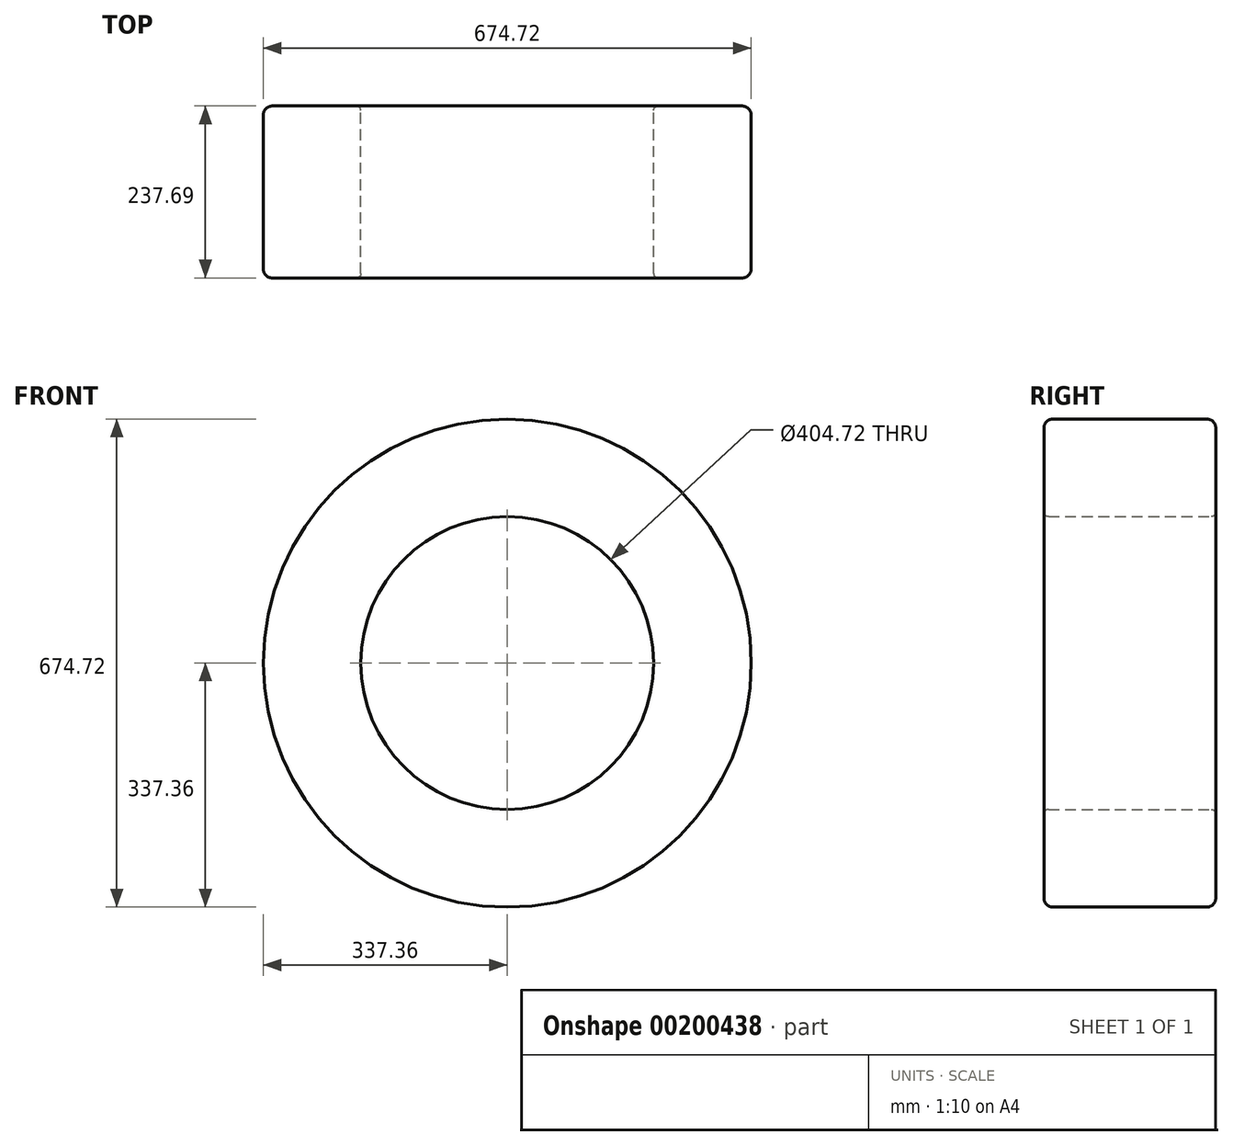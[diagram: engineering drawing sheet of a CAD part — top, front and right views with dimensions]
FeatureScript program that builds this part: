
annotation { "Feature Type Name" : "Feature", "Feature Type Description" : "" }
export const myFeature = defineFeature(function(context is Context, id is Id, definition is map)
    precondition{}
    {
        {
            var Q0;
            Q0=qCreatedBy(makeId("Front.planeOp"),FACE);
            var sketch = newSketch(context, id + "F0", { "sketchPlane" : qUnion([Q0])});
            skCircle(sketch, "E0", {"center": v(0, 0) * mm, "radius": 203.2 * mm});
            skSolve(sketch);
        }
        {
            var Q0;
            Q0=sQuery(id+"F0.wireOp",EDGE,"E0");
            extrude(context, id + "F1", {"bodyType" : ToolBodyType.SURFACE, "surfaceEntities" : qUnion([Q0]), "depth" : 225 * mm});
        }
        {
            var Q0;
            Q0=qCreatedBy(makeId("Right.planeOp"),FACE);
            var sketch = newSketch(context, id + "F2", { "sketchPlane" : qUnion([Q0])});
            skLineSegment(sketch, "E1.bottom", {"start": v(-229.51, 202.36) * mm, "end": v(8.18, 202.36) * mm});
            skLineSegment(sketch, "E1.top", {"start": v(-229.51, 337.36) * mm, "end": v(8.18, 337.36) * mm});
            skLineSegment(sketch, "E1.left", {"start": v(-229.51, 202.36) * mm, "end": v(-229.51, 337.36) * mm});
            skLineSegment(sketch, "E1.right", {"start": v(8.18, 202.36) * mm, "end": v(8.18, 337.36) * mm});
            skSolve(sketch);
        }
        {
            var Q0;
            Q0=makeQuery(id+"F2.imprint","IMPRINT",FACE,{"disambiguationData":[TD([[makeQuery(id+"F2.imprint","IMPRINT",EDGE,{"derivedFrom":sQuery(id+"F2.wireOp",EDGE,"E1.bottom")}),1.0]])]});
            var Q1;
            Q1=makeQuery(id+"F1.opExtrude","SWEPT_FACE",FACE,{"disambiguationData":[OSD([sQuery(id+"F0.wireOp",EDGE,"E0")])]});
            revolve(context, id + "F3", {"entities" : qUnion([Q0]), "axis" : qUnion([Q1]), "revolveType" : RevolveType.FULL});
        }
        {
            var Q0;
            Q0=makeQuery(id+"F3.opRevolve","SWEPT_EDGE",EDGE,{"disambiguationData":[OSD([sQuery(id+"F2.wireOp",EDGE,"E1.top"),sQuery(id+"F2.wireOp",EDGE,"E1.left")])]});
            fillet(context, id + "F4", {"entities" : qUnion([Q0]), "radius" : 12.7 * mm, "tangentPropagation" : true, "allowEdgeOverflow" : false});
        }
        {
            var Q0;
            Q0=makeQuery(id+"F3.opRevolve","SWEPT_EDGE",EDGE,{"disambiguationData":[OSD([sQuery(id+"F2.wireOp",EDGE,"E1.top"),sQuery(id+"F2.wireOp",EDGE,"E1.right")])]});
            fillet(context, id + "F5", {"entities" : qUnion([Q0]), "radius" : 12.7 * mm, "tangentPropagation" : true, "allowEdgeOverflow" : false});
        }
        {
            var Q0;
            Q0=makeQuery(id+"F3.opRevolve","SWEPT_EDGE",EDGE,{"disambiguationData":[OSD([sQuery(id+"F2.wireOp",EDGE,"E1.bottom"),sQuery(id+"F2.wireOp",EDGE,"E1.right")])]});
            fillet(context, id + "F6", {"entities" : qUnion([Q0]), "radius" : 6.35 * mm, "tangentPropagation" : true, "allowEdgeOverflow" : false});
        }
        {
            var Q0;
            Q0=makeQuery(id+"F3.opRevolve","SWEPT_EDGE",EDGE,{"disambiguationData":[OSD([sQuery(id+"F2.wireOp",EDGE,"E1.bottom"),sQuery(id+"F2.wireOp",EDGE,"E1.left")])]});
            fillet(context, id + "F7", {"entities" : qUnion([Q0]), "radius" : 6.35 * mm, "tangentPropagation" : true, "allowEdgeOverflow" : false});
        }
    });
